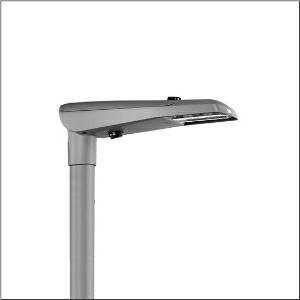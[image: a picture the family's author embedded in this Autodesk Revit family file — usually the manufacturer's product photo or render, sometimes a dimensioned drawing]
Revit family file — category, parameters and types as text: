
# Revit family: streetlight_sl_11_iq_micro___st1_2a_5xc1ac1y08de_0507
name_source: partatom
category: Lighting Fixtures
units: mm (PartAtom-declared; Revit-internal decimal feet)

## family parameters
Cut with Voids When Loaded = No
Host = Face
Light Source = No
Part Type = Normal
Room Calculation Point = No
Round Connector Dimension = Use Diameter
Shared = No

## types (1)
- --- (1 x LED, 3860 lm, 27.3 W, 4000K)
    Apparent Load = 27 VA
    CIE Flux Codes = 33 71 96 100 100
    Color Rendering = 70
    Color Temperature = 4000K
    Default Elevation = 1800 mm
    Description = Streetlight SL 11 iQ micro, mast luminaire, primary light control with 3 zone facetted reflector, of plastic, silver coated, highly specular, primary optical cover: cover, of PMMA, transparent, light distribution: ST1.2a, light emission: direct distribution, primary light characteristic: asymmetric, installation type: post-top, side-entry, lamps: LED, High Power LED, rated values: 3.620lm | 27,1W | 133,6lm/W (begin service life); end service life: 3.620lm | 27,6W; at 50% lumin. flux: 1.810lm | 13,3W | 136,1lm/W, colour temperature: 2200/2700/3000/4000K, colour rendering: CRI > 70, light colour: 722/727/730/740, light setting 1 begin service life: 100% | 3.620lm | 27,1W | 133,6lm/W | 3.000K, light setting 1 end service life: 27,6W, further light settings possible, control: pre-setting: logarithmic dimming characteristic, Street-Remote, Auto-Match, Temp-Guard, Lumen-Switch, Night-Set, Smart-Wire, Light-Fading, Desk-Remote (wireless, voltage-free reading and setting of iQ features in the workshop via application-optimized NFC function/RFID function), optimised constant luminous flux control (CLO 2.0), with cable H07RN-F 3x 1.5mm², mains connection: 220..240V, AC, 50/60Hz, connection cable pre-assembled, cable length: 6,5m, luminaire housing, of diecast aluminium, powder-coated, SITECO metallic grey (DB 702S), please order mast flange separately, inclination adjustable without tools: 0°, 5°, 10°, 15° (post-top) | 0°, -5°, -10°, -15° (side-entry), sealing non-destructively replaceable, multi-level sealing system, length: 600mm, width: 174mm, height: 116mm, mast flange for spigot size: 42mm (side-entry): 5XC10008XM4, 60/48mm (side-entry/post-top): 5XC10108XM2, 76/60mm (side-entry/post-top): 5XC10108XM1, equipment: Power, Smart Interface below and above, protection rating (complete): IP66, insulation class (complete): insulation class II (safety insulation), certification: CE, ENEC, ENEC+, VDE, UKCA, impact resistance: IK10, permissible operating ambient temperature for outdoor applications: -25..+50°C, standard-compliant lighting for roads and squares, Environmental Product Declaration (EPD) tested and certified by an independent institute, packaging unit: 1 piece

Light Distribution: ST1.2a
    Height = 116 mm
    Lamp = 1 x LED
    Lamp Light Flux = 3860 lm
    Lamp Power = 27.3 W
    Lamp count = 1
    Length = 600 mm
    Luminous efficacy = 141 lm/W
    Manufacturer = Siteco
    ModVariant = No
    Model = 5XC1AC1Y08DE
    Number of Poles = 1
    OnlyDefault = Yes
    Power Factor = 1
    Product Name = Streetlight SL 11 iQ micro | ST1.2a
    Product group = mast luminaire | pylon top
    ProductGroupID = 6100
    Protection Class = Protection class II
    Protection Degree = IP 66
    RLX_Detail_Level = 1
    RLX_Emergency_Light_Flux = 0 lm
    RLX_Emergency_Type = 0
    RLX_Emergency_Type_DB = No
    RlxData = <blob elided: 59365 chars, md5=1edecb21>
    Socket = socket
    Standby Power = 0 W
    System Light Flux = 3860 lm
    System Power = 27 W
    Type Comments = individual setting: luminous flux: 100 % | dim-lin: 254 | 726 mA
    Type Image = l_1005956.jpg
    URL = http://relux.com
    VarID = @adj_052089
    Voltage = 0 V
    Weight = 0.00 kg
    Width = 174 mm

## geometry (parser evidence)
native form markers: Blend x4, Sweep x12
no freeform markers — native parametric forms only
